# Revit family: Toilet-Floor_Outlet-Whitehall-BestCare-WH2142-ADA-T-3-EGE10_Series
name_source: partatom
category: Plumbing Fixtures
units: mm (PartAtom-declared; Revit-internal decimal feet)

## family parameters
Cut with Voids When Loaded = No
Host = Face
OmniClass Number = 23.45.05.21.11.11
OmniClass Title = Water Operated Water Closets
Part Type = Normal
Room Calculation Point = No
Round Connector Dimension = Use Diameter
Shared = Yes

## types (2) — shared parameters
-HET 1.28 Hydraulic GPF = No
-ULF 1.6 Hydraulic GPF = No
ADA Compliant = Yes
Assembly Code = D2010110
Body Material = Stainless Steel-Whitehall-Powder Coated White
Bowl Shape = Elongated
CW Connection = Yes
CWFU = 5
Compliance Certifications = The toilet is compliant to ADA 2010, ASME A112.19.3 and CSA B45.4.
Default Elevation = 0"
Description = BestCare® Ligature-Resistant, ADA Compliant Toilet, On-Floor, Top Supply
Flush Rate = 1.28 gpf
HW Connection = No
Height = 18 3/8"
Installation Type = Floor Mounted
Length = 29 1/4"
Load Rating = 5000 lbs.
Manufacturer = Whitehall Mfg
Minimum Flowing Pressure = 25.00 psi
Product Documentation Link = https://www.whitehallmfg.com
Product Page URL = https://www.whitehallmfg.com
Revised Date = 08/18/2023
Seat Cover Material = Stainless_Steel-Whitehall-WH-LRSC-GRAY
URL = http://www.whitehallmfg.com
Vent Connection = No
WFU = 5
WH-LRSC-BLACK Ligature Resistant Seat Cover, Black (Shipped Loose) = No
WH-LRSC-BLUE Ligature Resistant Seat Cover, Dignity Blue (Shipped Loose) = No
WH-LRSC-WHITE Ligature Resistant Seat Cover, White (Shipped Loose) = No
Waste Connection = Yes
Waste Connection Diameter = 7 1/2"
Waste Connection Height = 5 1/2"
Waste Connection Radius = 3 3/4"
Width = 14 3/4"
cUPC Compliant = Yes
zero-valued in all types: HWFU

## per-type parameters (varying)
| type | Waste Connection Distance From Wall |
| WH2142-ADA-T-3-EGE10_10 | 10" |
| WH2142-ADA-T-3-EGE10_12 | 12" |

note: column(s) folded — value = type name in every type: Model

## geometry (parser evidence)
native form markers: Sweep x4
no freeform markers — native parametric forms only
